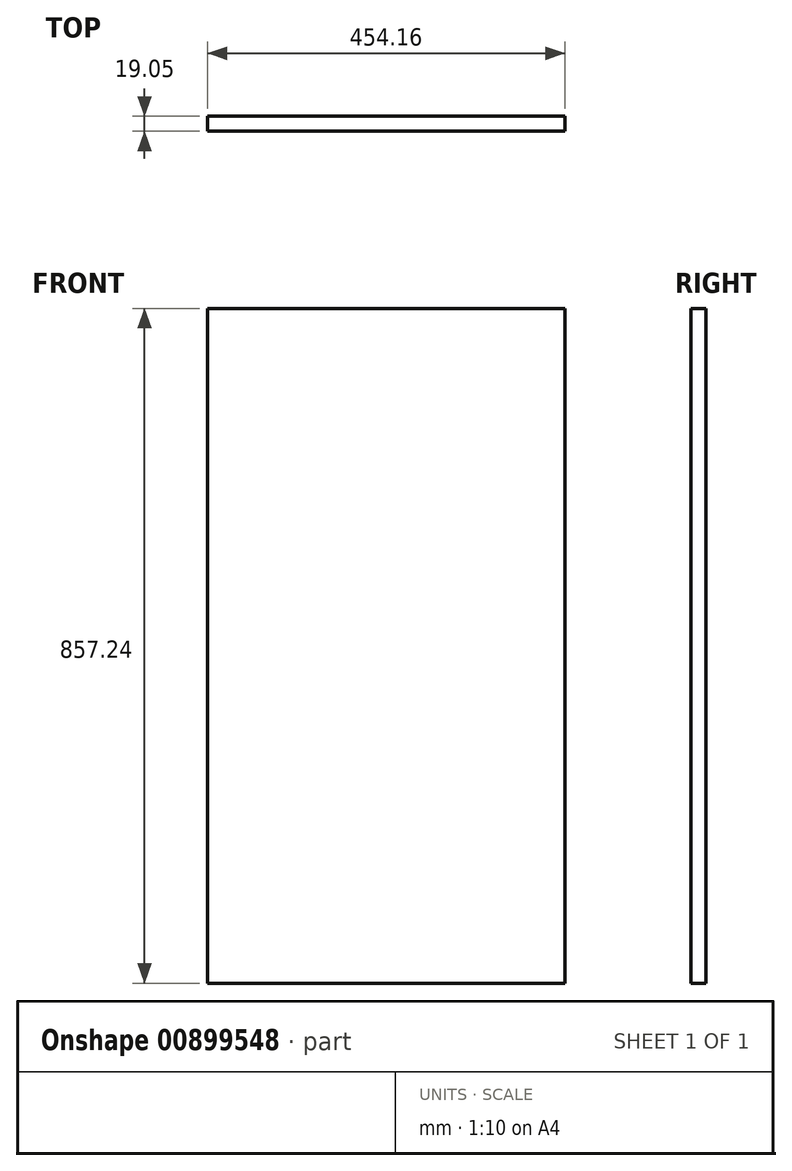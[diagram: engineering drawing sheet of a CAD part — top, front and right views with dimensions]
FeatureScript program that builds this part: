
annotation { "Feature Type Name" : "Feature", "Feature Type Description" : "" }
export const myFeature = defineFeature(function(context is Context, id is Id, definition is map)
    precondition{}
    {
        {
            var Q0;
            Q0=qCreatedBy(makeId("Front.planeOp"),FACE);
            var sketch = newSketch(context, id + "F0", { "sketchPlane" : qUnion([Q0])});
            skLineSegment(sketch, "E0.bottom", {"start": v(227.08, 428.63) * mm, "end": v(-227.08, 428.63) * mm});
            skLineSegment(sketch, "E0.top", {"start": v(227.08, -428.63) * mm, "end": v(-227.08, -428.63) * mm});
            skLineSegment(sketch, "E0.left", {"start": v(227.08, 428.63) * mm, "end": v(227.08, -428.63) * mm});
            skLineSegment(sketch, "E0.right", {"start": v(-227.08, 428.63) * mm, "end": v(-227.08, -428.63) * mm});
            skPoint(sketch, "E0.middle", {"position": v(0, 0) * mm});
            skSolve(sketch);
        }
        {
            var Q0;
            Q0=makeQuery(id+"F0.imprint","IMPRINT",FACE,{"disambiguationData":[TD([[makeQuery(id+"F0.imprint","IMPRINT",EDGE,{"derivedFrom":sQuery(id+"F0.wireOp",EDGE,"E0.bottom")}),1.0]])]});
            extrude(context, id + "F1", {"entities" : qUnion([Q0]), "depth" : 19.05 * mm, "offsetDistance" : 25.4 * mm});
        }
    });
